# Revit family: Haworth_Masters_FreestandingStorageUnit
name_source: partatom
category: Furniture Systems
revit_build: Autodesk Revit 2018 (Build: 20170223_1515(x64)
units: mm (PartAtom-declared; Revit-internal decimal feet)

## family parameters
Always vertical = Yes
Cut with Voids When Loaded = No
OmniClass Number = 23.40.70.14.64.21
OmniClass Title = Systems Furniture
Part Type = Normal
Room Calculation Point = No
Round Connector Dimension = Use Diameter
Shared = No
Work Plane-Based = No

## types (8) — shared parameters
Actual Height = 41 5/8"
Assembly Code = E2020200
Bar Pull = No
Classic Pull = Yes
Drawer Height = 39 1/16"
Finger Pull = No
Linear Pull = No
Manufacturer = Haworth
Max. Depth = 24"
Max. Width = 36"
Min. Depth = 19"
Min. Width = 30"
Model = Haworth Masters
Revision Number = 1
Shelf Spacing = 12 25/32"
Size = Verify Final Dim. w/ Haworth
Standard Widths = 30, 36 in.
Sustainability Info = https://www.haworth.com
URL = http://www.haworth.com
URL - Product = https://www.haworth.com
Warranty = http://www.haworth.com

## per-type parameters (varying)
| type | Actual Depth | Actual Width | Custom Size | Depth | Description | Door Width | Doors | Drawer Depth | Drawer Width | Open | Width |
| 19d 36w 41h - Open | 19" | 36" | Yes | 0" | Haworth  - Masters - Freestanding - Open Storage Unit - 19d 36w 41h | 18" | No | 17 13/32" | 34 1/2" | Yes | 36" |
| 19d 30w 41h - Open | 19" | 30" | No | 19" | Haworth  - Masters - Freestanding - Open Storage Unit - 19d 30w 41h | 15" | No | 17 13/32" | 28 1/2" | Yes | 30" |
| 24d 30w 41h - Open | 24" | 30" | No | 24" | Haworth  - Masters - Freestanding - Open Storage Unit - 24d 30w 41h | 15" | No | 22 13/32" | 28 1/2" | Yes | 30" |
| 24d 36w 41h - Open | 24" | 36" | No | 24" | Haworth  - Masters - Freestanding - Open Storage Unit - 24d 36w 41h | 18" | No | 22 13/32" | 34 1/2" | Yes | 36" |
| 24d 36w 41h - Hinged Doors | 24" | 36" | No | 24" | Haworth  - Masters - Freestanding - Storage Unit with Hinged Doors - 24d 36w 41h | 18" | Yes | 22 13/32" | 34 1/2" | No | 36" |
| 24d 30w 41h - Hinged Doors | 24" | 30" | No | 24" | Haworth  - Masters - Freestanding - Storage Unit with Hinged Doors - 24d 30w 41h | 15" | Yes | 22 13/32" | 28 1/2" | No | 30" |
| 19d 36w 41h - Hinged Doors | 19" | 36" | No | 19" | Haworth  - Masters - Freestanding - Storage Unit with Hinged Doors - 19d 36w 41h | 18" | Yes | 17 13/32" | 34 1/2" | No | 36" |
| 19d 30w 41h - Hinged Doors | 19" | 30" | No | 19" | Haworth  - Masters - Freestanding - Storage Unit with Hinged Doors - 19d 30w 41h | 15" | Yes | 17 13/32" | 28 1/2" | No | 30" |

## geometry (parser evidence)
native form markers: Sweep x6
no freeform markers — native parametric forms only
